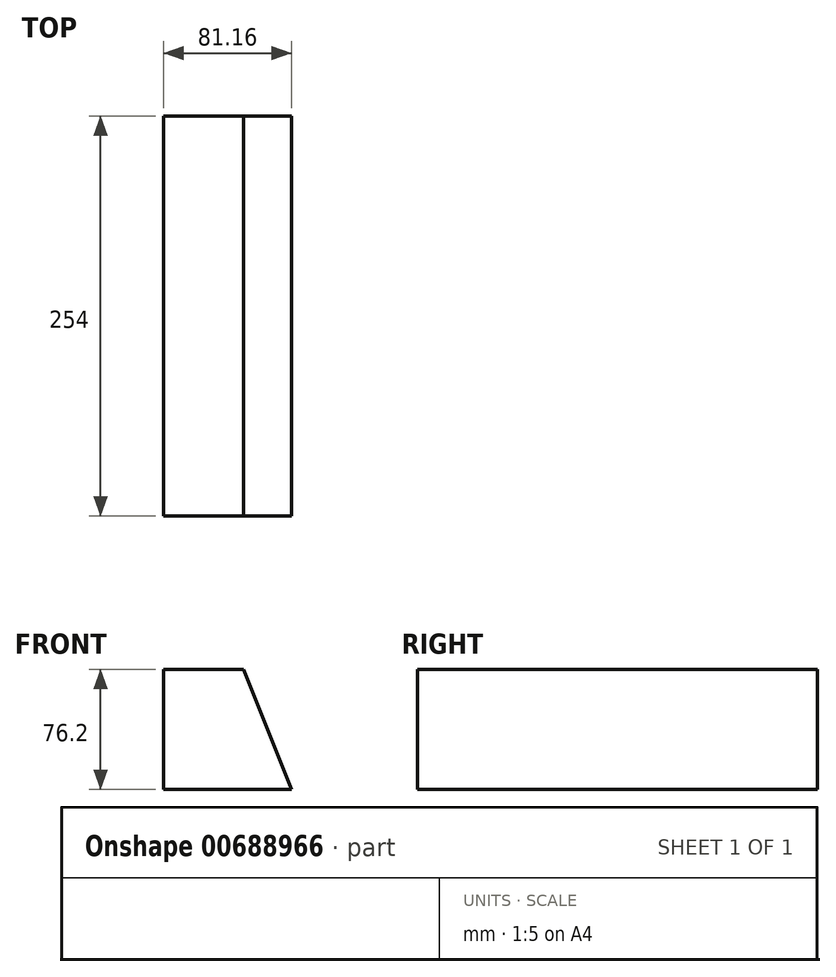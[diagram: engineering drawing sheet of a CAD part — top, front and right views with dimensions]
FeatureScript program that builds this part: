
annotation { "Feature Type Name" : "Feature", "Feature Type Description" : "" }
export const myFeature = defineFeature(function(context is Context, id is Id, definition is map)
    precondition{}
    {
        {
            var Q0;
            Q0=qCreatedBy(makeId("Front.planeOp"),FACE);
            var sketch = newSketch(context, id + "F0", { "sketchPlane" : qUnion([Q0])});
            skLineSegment(sketch, "E0", {"start": v(17.28, 39.87) * mm, "end": v(-33.52, 39.87) * mm});
            skLineSegment(sketch, "E1", {"start": v(-33.52, -36.33) * mm, "end": v(-33.52, 39.87) * mm});
            skLineSegment(sketch, "E2", {"start": v(-33.52, -36.33) * mm, "end": v(47.64, -36.33) * mm});
            skLineSegment(sketch, "E3", {"start": v(47.64, -36.33) * mm, "end": v(17.28, 39.87) * mm});
            skSolve(sketch);
        }
        {
            var Q0;
            Q0=makeQuery(id+"F0.imprint","IMPRINT",FACE,{"disambiguationData":[TD([[makeQuery(id+"F0.imprint","IMPRINT",EDGE,{"derivedFrom":sQuery(id+"F0.wireOp",EDGE,"E0")}),1.0]])]});
            extrude(context, id + "F1", {"entities" : qUnion([Q0]), "depth" : 254 * mm, "offsetDistance" : 25.4 * mm});
        }
    });
